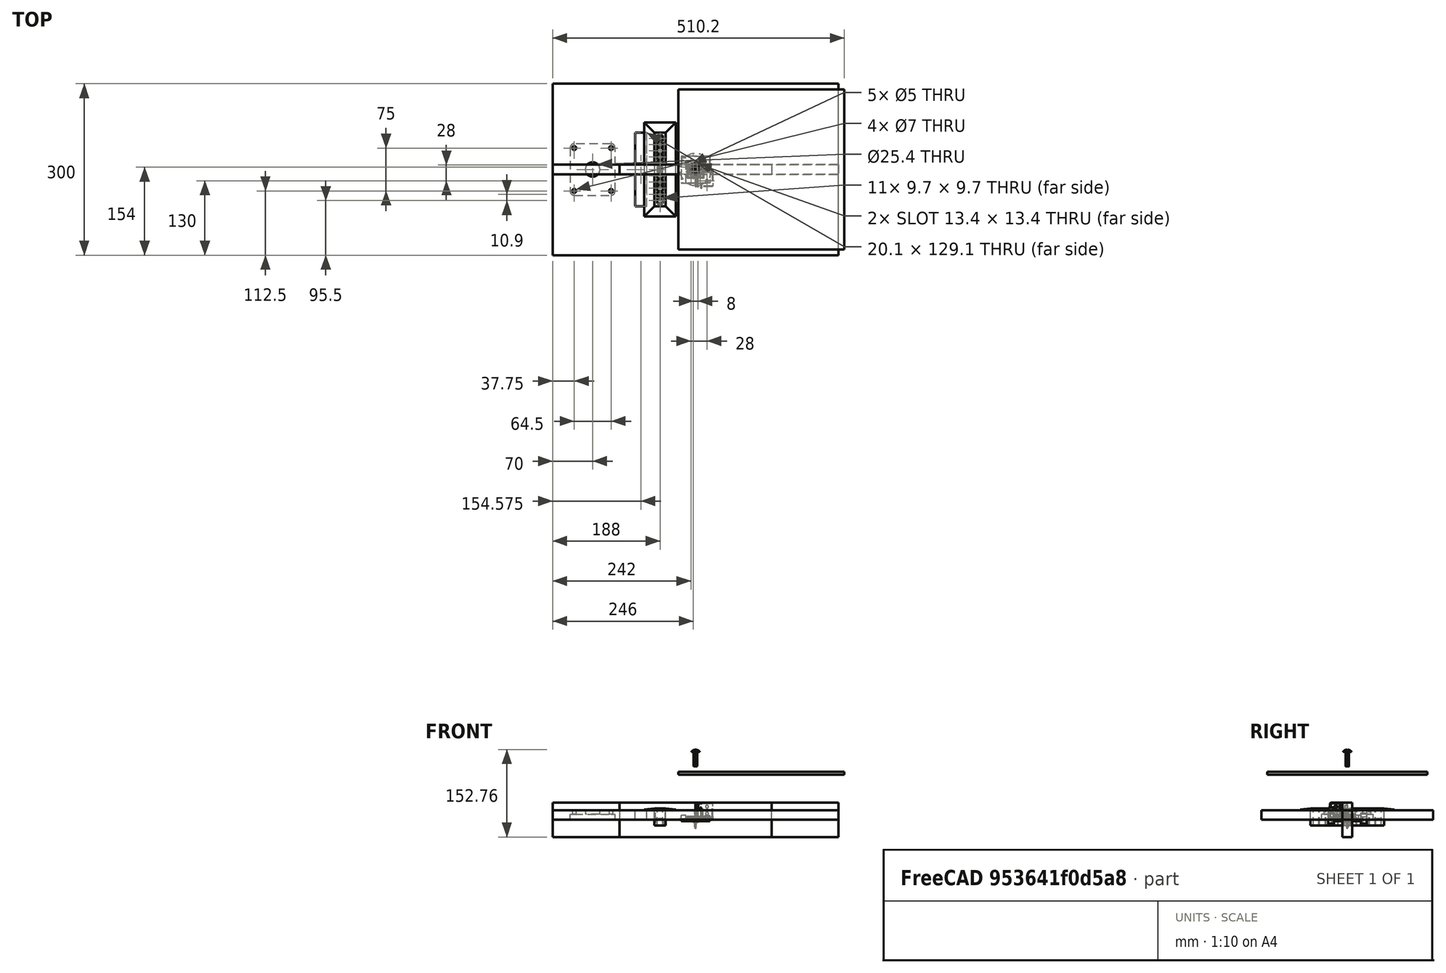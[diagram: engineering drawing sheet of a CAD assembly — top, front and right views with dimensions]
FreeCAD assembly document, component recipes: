
FREECAD ASSEMBLY — COMPONENT RECIPES ("BoxV2")

This assembly document has 71 components, labeled P0..P70 below (a component is one placed body or linked part). 9 of them carry a construction recipe — the FreeCAD feature program that regenerates the part from scratch, quoted from this document or its linked companion documents; the rest are supplied as boundary geometry only. No exploded tour is included for this assembly.
COMPONENT P0 — geometry summary ("Box_Cover002"; no construction recipe available for this part):
  bounding box: 500.0 x 300.0 x 17.0 mm
  tessellated surface: 2,508 triangles
  volume: 2430978 mm^3 (95% of its bounding box)
  symmetry: mirror-symmetric across its y mid-plane
COMPONENT P1 — recipe-attached ("Bracket002", modeled in this document).
Construction recipe (the document's own serialized feature program — sketch geometry with constraints, then the solid features built on it; lengths are millimeters unless a unit is written):

FEATURE [Sketcher::SketchObject] Sketch
  ArcFitTolerance = 1e-06
  AttachmentSupport = -> [XY_Plane]
  FullyConstrained = true
  MakeInternals = false
  MapMode = 5
  sketch-geometry (4):
    g0: LineSegment StartX=0 StartY=0 StartZ=0 EndX=30 EndY=0 EndZ=0
    g1: LineSegment StartX=30 StartY=0 StartZ=0 EndX=30 EndY=-30 EndZ=0
    g2: LineSegment StartX=30 StartY=-30 StartZ=0 EndX=0 EndY=-30 EndZ=0
    g3: LineSegment StartX=0 StartY=-30 StartZ=0 EndX=0 EndY=0 EndZ=0
  constraints (11):
    c: Coincident(g0,g1)
    c: Coincident(g1,g2)
    c: Coincident(g2,g3)
    c: Coincident(g3,g0)
    c: Horizontal(g0)
    c: Horizontal(g2)
    c: Vertical(g1)
    c: Vertical(g3)
    c: Distance(g1,g3) = 30
    c: Coincident(g0,g-1)
    c: DistanceY(g1,g1) = 30
FEATURE [PartDesign::Pad] Pad
  Direction = (0,0,1)
  Length = 30
  Length2 = 10
  Profile = -> Sketch
  ReferenceAxis = -> Sketch [N_Axis]
  Refine = true
  Suppressed = false
  Type = 0
FEATURE [PartDesign::Thickness] Thickness
  Base = -> Pad [Face2,Face3,Face6]
  BaseFeature = -> Pad
  Intersection = false
  Join = 0
  Mode = 0
  Refine = true
  Reversed = true
  SupportTransform = false
  Suppressed = false
  Value = 4
FEATURE [Sketcher::SketchObject] Sketch001
  ArcFitTolerance = 1e-06
  AttachmentOffset = pos=(0,2,0) rot=(0,0,1;0rad)
  AttachmentSupport = -> [YZ_Plane]
  FullyConstrained = true
  MakeInternals = false
  MapMode = 5
  Placement = pos=(0,0,2) rot=(0.57735,0.57735,0.57735;2.0944rad)
  expr: Constraints[1] = <<LHProperties>>.screw_diameter
  sketch-geometry (8):
    g0: Circle CenterX=-20 CenterY=21 CenterZ=0 NormalX=0 NormalY=0 NormalZ=1 AngleXU=0 Radius=2.5
    g1: Circle CenterX=-20 CenterY=9 CenterZ=0 NormalX=0 NormalY=0 NormalZ=1 AngleXU=0 Radius=2.5
    g2: LineSegment [constr] StartX=0 StartY=0 StartZ=0 EndX=0 EndY=30 EndZ=0
    g3: LineSegment [constr] StartX=0 StartY=30 StartZ=0 EndX=-30 EndY=30 EndZ=0
    g4: LineSegment [constr] StartX=-30 StartY=30 StartZ=0 EndX=-30 EndY=0 EndZ=0
    g5: LineSegment [constr] StartX=-30 StartY=0 StartZ=0 EndX=0 EndY=0 EndZ=0
    g6: LineSegment [constr] StartX=-20 StartY=21 StartZ=0 EndX=-20 EndY=30 EndZ=0
    g7: LineSegment [constr] StartX=-20 StartY=9 StartZ=0 EndX=-20 EndY=0 EndZ=0
  constraints (23):
    c: Equal(g1,g0)
    c: Diameter(g0) = 5
    c: Vertical(g0,g1)
    c: DistanceX(g1) = -20
    c: Coincident(g2,g3)
    c: Coincident(g3,g4)
    c: Coincident(g4,g5)
    c: Coincident(g5,g2)
    c: Vertical(g2)
    c: Vertical(g4)
    c: Horizontal(g3)
    c: Horizontal(g5)
    c: Coincident(g2,g-1)
    c: DistanceX(g3,g3) = 30
    c: DistanceY(g4,g4) = 30
    c: Coincident(g6,g0)
    c: PointOnObject(g6,g3)
    c: Vertical(g6)
    c: Coincident(g7,g1)
    c: PointOnObject(g7,g5)
    c: Vertical(g7)
    c: Equal(g7,g6)
    c: DistanceY(g1,g0) = 12
FEATURE [PartDesign::Pocket] Pocket
  BaseFeature = -> Thickness
  Direction = (-1,0,0)
  Length = 10
  Length2 = 5
  Midplane = true
  Profile = -> Sketch001
  ReferenceAxis = -> Sketch001 [N_Axis]
  Refine = true
  Suppressed = false
  Type = 0
FEATURE [PartDesign::PolarPattern] PolarPattern
  Angle = 90
  Axis = -> Sketch001 [V_Axis]
  BaseFeature = -> Pocket
  Mode = 0
  Occurrences = 2
  Offset = 120
  Originals = -> [Pocket]
  Refine = true
  Suppressed = false
  TransformMode = 0
FEATURE [PartDesign::SubtractiveCylinder] Cylinder
  Angle = 360
  AttacherType = Attacher::AttachEngine3D
  AttachmentOffset = pos=(20,-20,0) rot=(0,0,1;0rad)
  AttachmentSupport = -> [XY_Plane]
  BaseFeature = -> PolarPattern
  FirstAngle = 0
  Height = 10
  MapMode = 5
  Placement = pos=(20,-20,0) rot=(0,0,1;0rad)
  Radius = 2.5
  Refine = true
  SecondAngle = 0
  Suppressed = false
  expr: Radius = <<LHProperties>>.screw_diameter / 2
FEATURE [PartDesign::Chamfer] Chamfer
  Angle = 45
  Base = -> Cylinder [Edge35]
  BaseFeature = -> Cylinder
  ChamferType = 0
  FlipDirection = false
  Placement = pos=(20,-20,0) rot=(0,0,1;0rad)
  Refine = true
  Size = 8
  Size2 = 1
  SupportTransform = false
  Suppressed = false
  UseAllEdges = false
FEATURE [PartDesign::Chamfer] Chamfer001
  Angle = 45
  Base = -> Chamfer [Edge1,Edge2,Edge3,Edge4,Edge6,Edge8,Edge9,Edge10,Edge13,Edge14,Edge15,Edge16,Edge19,Edge20,Edge23,Edge24,Edge27,Edge30,Edge34,Edge35,Edge37,Edge38,Edge39]
  BaseFeature = -> Chamfer
  ChamferType = 0
  FlipDirection = false
  Placement = pos=(20,-20,0) rot=(0,0,1;0rad)
  Refine = true
  Size = 1
  Size2 = 1
  SupportTransform = false
  Suppressed = false
  UseAllEdges = false
FEATURE [PartDesign::Body] Body  label="Bracket"
  AllowCompound = false
  Group = -> [Sketch,Pad,Thickness,Sketch001,Pocket,PolarPattern,Cylinder,Chamfer,Chamfer001]
  Origin = -> Origin
  Tip = -> Chamfer001
COMPONENT P2 — same part as P1; its construction recipe is shown at P1.
COMPONENT P3 — same part as P1; its construction recipe is shown at P1.
COMPONENT P4 — same part as P1; its construction recipe is shown at P1.
COMPONENT P5 — recipe-attached ("Cable_Management002", modeled in this document).
Construction recipe (the document's own serialized feature program — sketch geometry with constraints, then the solid features built on it; lengths are millimeters unless a unit is written):

FEATURE [Sketcher::SketchObject] Sketch027
  ArcFitTolerance = 1e-06
  AttachmentSupport = -> [XY_Plane015]
  FullyConstrained = true
  MakeInternals = false
  MapMode = 5
  expr: Constraints[11] = <<CMProperties>>.cm_size
  sketch-geometry (5):
    g0: LineSegment StartX=-15 StartY=-15 StartZ=0 EndX=15 EndY=-15 EndZ=0
    g1: LineSegment StartX=15 StartY=-15 StartZ=0 EndX=15 EndY=15 EndZ=0
    g2: LineSegment StartX=15 StartY=15 StartZ=0 EndX=-15 EndY=15 EndZ=0
    g3: LineSegment StartX=-15 StartY=15 StartZ=0 EndX=-15 EndY=-15 EndZ=0
    g4: GeomPoint [constr] X=-1e-16 Y=0 Z=0
  constraints (12):
    c: Coincident(g0,g1)
    c: Coincident(g1,g2)
    c: Coincident(g2,g3)
    c: Coincident(g3,g0)
    c: Horizontal(g0)
    c: Horizontal(g2)
    c: Vertical(g1)
    c: Vertical(g3)
    c: Symmetric(g2,g0,g4)
    c: Coincident(g4,g-1)
    c: Equal(g2,g1)
    c: DistanceX(g2,g2) = 30
FEATURE [PartDesign::Pad] Pad013
  Direction = (0,0,1)
  Length = 4.7
  Length2 = 10
  Profile = -> Sketch027
  ReferenceAxis = -> Sketch027 [N_Axis]
  Refine = true
  Suppressed = false
  Type = 0
  expr: Length = <<CMProperties>>.cm_height + <<CMProperties>>.cm_base_height
FEATURE [Sketcher::SketchObject] Sketch028
  ArcFitTolerance = 1e-06
  AttachmentOffset = pos=(0,0,1.2) rot=(0,0,1;0rad)
  AttachmentSupport = -> [XY_Plane015]
  FullyConstrained = true
  MakeInternals = false
  MapMode = 5
  Placement = pos=(0,0,1.2) rot=(0,0,1;0rad)
  expr: .AttachmentOffset.Base.z = <<CMProperties>>.cm_base_height
  expr: Constraints[10] = <<CMProperties>>.cm_size / 2
  expr: Constraints[34] = <<CMProperties>>.cm_track_size
  expr: Constraints[9] = <<CMProperties>>.cm_size / 2
  sketch-geometry (19):
    g0: ArcOfCircle [constr] CenterX=-6 CenterY=6.01432 CenterZ=0 NormalX=0 NormalY=0 NormalZ=1 AngleXU=0 Radius=6.01432 StartAngle=4.71239 EndAngle=6.21417
    g1: ArcOfCircle [constr] CenterX=5.2375 CenterY=5.2375 CenterZ=0 NormalX=0 NormalY=0 NormalZ=1 AngleXU=0 Radius=5.25 StartAngle=4.78141 EndAngle=9.35576
    g2: LineSegment [constr] StartX=-6 StartY=0 StartZ=0 EndX=-15 EndY=0 EndZ=0
    g3: ArcOfCircle [constr] CenterX=6.01432 CenterY=-6 CenterZ=0 NormalX=0 NormalY=0 NormalZ=1 AngleXU=0 Radius=6.01432 StartAngle=1.63981 EndAngle=3.14159
    g4: LineSegment [constr] StartX=0 StartY=-6 StartZ=0 EndX=0 EndY=-15 EndZ=0
    g5: ArcOfCircle [constr] CenterX=-15 CenterY=0 CenterZ=0 NormalX=0 NormalY=0 NormalZ=-1 AngleXU=-3.14159 Radius=1.75 StartAngle=1.5708 EndAngle=4.71239
    g6: LineSegment StartX=-6 StartY=1.75 StartZ=0 EndX=-15 EndY=1.75 EndZ=0
    g7: ArcOfCircle CenterX=-6 CenterY=6.01432 CenterZ=0 NormalX=0 NormalY=0 NormalZ=1 AngleXU=0 Radius=4.26432 StartAngle=4.71239 EndAngle=6.21417
    g8: ArcOfCircle CenterX=5.2375 CenterY=5.2375 CenterZ=0 NormalX=0 NormalY=0 NormalZ=1 AngleXU=0 Radius=7 StartAngle=4.78141 EndAngle=9.35576
    g9: ArcOfCircle CenterX=6.01432 CenterY=-6 CenterZ=0 NormalX=0 NormalY=0 NormalZ=1 AngleXU=0 Radius=4.26432 StartAngle=1.63981 EndAngle=3.14159
    g10: LineSegment StartX=1.75 StartY=-6 StartZ=0 EndX=1.75 EndY=-15 EndZ=0
    g11: ArcOfCircle [constr] CenterX=0 CenterY=-15 CenterZ=0 NormalX=0 NormalY=0 NormalZ=-1 AngleXU=1.5708 Radius=1.75 StartAngle=1.5708 EndAngle=4.71239
    g12: LineSegment StartX=-1.75 StartY=-6 StartZ=0 EndX=-1.75 EndY=-15 EndZ=0
    g13: ArcOfCircle CenterX=6.01432 CenterY=-6 CenterZ=0 NormalX=0 NormalY=0 NormalZ=1 AngleXU=0 Radius=7.76432 StartAngle=1.63981 EndAngle=3.14159
    g14: ArcOfCircle CenterX=5.2375 CenterY=5.2375 CenterZ=0 NormalX=0 NormalY=0 NormalZ=1 AngleXU=0 Radius=3.5 StartAngle=4.78141 EndAngle=9.35576
    g15: ArcOfCircle CenterX=-6 CenterY=6.01432 CenterZ=0 NormalX=0 NormalY=0 NormalZ=1 AngleXU=0 Radius=7.76432 StartAngle=4.71239 EndAngle=6.21417
    g16: LineSegment StartX=-6 StartY=-1.75 StartZ=0 EndX=-15 EndY=-1.75 EndZ=0
    g17: LineSegment StartX=1.75 StartY=-15 StartZ=0 EndX=-1.75 EndY=-15 EndZ=0
    g18: LineSegment StartX=-15 StartY=1.75 StartZ=0 EndX=-15 EndY=-1.75 EndZ=0
  constraints (43):
    c: PointOnObject(g0,g-1)
    c: PointOnObject(g0,g-2)
    c: Tangent(g1,g0) = 1.5708
    c: PointOnObject(g2,g-1)
    c: Tangent(g2,g0) = 1.5708
    c: Vertical(g4)
    c: Tangent(g4,g3) = -1.5708
    c: Tangent(g3,g1) = 1.5708
    c: Vertical(g3,g-1)
    c: DistanceY(g4,g-1) = 15
    c: DistanceX(g2,g-1) = 15
    c: Tangent(g5,g6) = -1.5708
    c: Tangent(g5,g16) = 1.5708
    c: Tangent(g6,g7) = 1.5708
    c: Tangent(g7,g8) = 1.5708
    c: Tangent(g8,g9) = 1.5708
    c: Tangent(g9,g10) = -1.5708
    c: Tangent(g10,g11) = 1.5708
    c: Tangent(g11,g12) = -1.5708
    c: Tangent(g12,g13) = -1.5708
    c: Tangent(g13,g14) = 1.5708
    c: Tangent(g14,g15) = 1.5708
    c: Tangent(g15,g16) = 1.5708
    c: Coincident(g5,g2)
    c: Coincident(g1,g14)
    c: Coincident(g8,g1)
    c: Coincident(g0,g7)
    c: Coincident(g0,g15)
    c: Coincident(g3,g9)
    c: Coincident(g3,g13)
    c: Coincident(g11,g4)
    c: Horizontal(g10,g4)
    c: Horizontal(g11,g4)
    c: Vertical(g5,g2)
    c: DistanceY(g5,g5) = 3.5
    c: Equal(g6,g10)
    c: DistanceX(g0,g3) = 6
    c: Equal(g13,g15)
    c: Radius(g8) = 7
    c: Coincident(g17,g10)
    c: Coincident(g17,g11)
    c: Coincident(g18,g5)
    c: Coincident(g18,g5)
FEATURE [PartDesign::Pocket] Pocket011
  BaseFeature = -> Pad013
  Direction = (0,0,-1)
  Length = 5
  Length2 = 5
  Profile = -> Sketch028
  ReferenceAxis = -> Sketch028 [N_Axis]
  Refine = true
  Reversed = true
  Suppressed = false
  Type = 1
FEATURE [Sketcher::SketchObject] Sketch029
  ArcFitTolerance = 1e-06
  AttachmentOffset = pos=(0,0,4.7) rot=(0,0,1;0rad)
  AttachmentSupport = -> [XY_Plane015]
  FullyConstrained = true
  MakeInternals = false
  MapMode = 5
  Placement = pos=(0,0,4.7) rot=(0,0,1;0rad)
  expr: .AttachmentOffset.Base.z = <<CMProperties>>.cm_base_height + <<CMProperties>>.cm_height
  expr: Constraints[11] = Sketch027.Constraints[11]
  expr: Constraints[31] = Sketch028.Constraints[9]
  expr: Constraints[32] = Sketch028.Constraints[10]
  expr: Constraints[55] = <<CMProperties>>.cm_track_size
  sketch-geometry (41):
    g0: LineSegment [constr] StartX=-15 StartY=-15 StartZ=0 EndX=15 EndY=-15 EndZ=0
    g1: LineSegment [constr] StartX=15 StartY=-15 StartZ=0 EndX=15 EndY=15 EndZ=0
    g2: LineSegment [constr] StartX=15 StartY=15 StartZ=0 EndX=-15 EndY=15 EndZ=0
    g3: LineSegment [constr] StartX=-15 StartY=15 StartZ=0 EndX=-15 EndY=-15 EndZ=0
    g4: GeomPoint [constr] X=0 Y=0 Z=0
    g5: LineSegment StartX=15 StartY=-15 StartZ=0 EndX=15 EndY=15 EndZ=0
    g6: LineSegment StartX=15 StartY=15 StartZ=0 EndX=-15 EndY=15 EndZ=0
    g7: LineSegment StartX=13.4 StartY=-13.4 StartZ=0 EndX=13.4 EndY=13.4 EndZ=0
    g8: LineSegment StartX=13.4 StartY=13.4 StartZ=0 EndX=-13.4 EndY=13.4 EndZ=0
    g9: GeomPoint [constr] X=0 Y=0 Z=0
    g10: ArcOfCircle [constr] CenterX=-8 CenterY=8.06933 CenterZ=0 NormalX=0 NormalY=0 NormalZ=1 AngleXU=0 Radius=8.06933 StartAngle=4.71239 EndAngle=6.15201
    g11: ArcOfCircle [constr] CenterX=6.1963 CenterY=6.1963 CenterZ=0 NormalX=0 NormalY=0 NormalZ=1 AngleXU=0 Radius=6.25 StartAngle=4.84357 EndAngle=9.2936
    g12: LineSegment [constr] StartX=-8 StartY=0 StartZ=0 EndX=-15 EndY=0 EndZ=0
    g13: ArcOfCircle [constr] CenterX=8.06933 CenterY=-8 CenterZ=0 NormalX=0 NormalY=0 NormalZ=1 AngleXU=0 Radius=8.06933 StartAngle=1.70198 EndAngle=3.14159
    g14: LineSegment [constr] StartX=0 StartY=-8 StartZ=0 EndX=0 EndY=-15 EndZ=0
    g15: ArcOfCircle [constr] CenterX=-15 CenterY=0 CenterZ=0 NormalX=0 NormalY=0 NormalZ=-1 AngleXU=-3.14159 Radius=1.75 StartAngle=1.5708 EndAngle=4.71239
    g16: LineSegment [constr] StartX=-8 StartY=1.75 StartZ=0 EndX=-15 EndY=1.75 EndZ=0
    g17: ArcOfCircle [constr] CenterX=-8 CenterY=8.06933 CenterZ=0 NormalX=0 NormalY=0 NormalZ=1 AngleXU=0 Radius=6.31933 StartAngle=4.71239 EndAngle=6.15201
    g18: ArcOfCircle [constr] CenterX=6.1963 CenterY=6.1963 CenterZ=0 NormalX=0 NormalY=0 NormalZ=1 AngleXU=0 Radius=8 StartAngle=4.84357 EndAngle=9.2936
    g19: ArcOfCircle [constr] CenterX=8.06933 CenterY=-8 CenterZ=0 NormalX=0 NormalY=0 NormalZ=1 AngleXU=0 Radius=6.31933 StartAngle=1.70198 EndAngle=3.14159
    g20: LineSegment [constr] StartX=1.75 StartY=-8 StartZ=0 EndX=1.75 EndY=-15 EndZ=0
    g21: ArcOfCircle [constr] CenterX=0 CenterY=-15 CenterZ=0 NormalX=0 NormalY=0 NormalZ=-1 AngleXU=1.5708 Radius=1.75 StartAngle=1.5708 EndAngle=4.71239
    g22: LineSegment [constr] StartX=-1.75 StartY=-8 StartZ=0 EndX=-1.75 EndY=-15 EndZ=0
    g23: ArcOfCircle [constr] CenterX=8.06933 CenterY=-8 CenterZ=0 NormalX=0 NormalY=0 NormalZ=1 AngleXU=0 Radius=9.81933 StartAngle=1.70198 EndAngle=3.14159
    g24: ArcOfCircle [constr] CenterX=6.1963 CenterY=6.1963 CenterZ=0 NormalX=0 NormalY=0 NormalZ=1 AngleXU=0 Radius=4.5 StartAngle=4.84357 EndAngle=9.2936
    g25: ArcOfCircle [constr] CenterX=-8 CenterY=8.06933 CenterZ=0 NormalX=0 NormalY=0 NormalZ=1 AngleXU=0 Radius=9.81933 StartAngle=4.71239 EndAngle=6.15201
    g26: LineSegment [constr] StartX=-8 StartY=-1.75 StartZ=0 EndX=-15 EndY=-1.75 EndZ=0
    g27: LineSegment [constr] StartX=1.75 StartY=-15 StartZ=0 EndX=-1.75 EndY=-15 EndZ=0
    g28: LineSegment [constr] StartX=-15 StartY=1.75 StartZ=0 EndX=-15 EndY=-1.75 EndZ=0
    g29: LineSegment StartX=-15 StartY=1.75 StartZ=0 EndX=-13.4 EndY=1.75 EndZ=0
    g30: LineSegment StartX=13.4 StartY=-13.4 StartZ=0 EndX=1.75 EndY=-13.4 EndZ=0
    g31: LineSegment StartX=15 StartY=-15 StartZ=0 EndX=1.75 EndY=-15 EndZ=0
    g32: LineSegment StartX=-1.75 StartY=-15 StartZ=0 EndX=-15 EndY=-15 EndZ=0
    g33: LineSegment StartX=-15 StartY=-15 StartZ=0 EndX=-15 EndY=-1.75 EndZ=0
    g34: LineSegment StartX=-15 StartY=1.75 StartZ=0 EndX=-15 EndY=15 EndZ=0
    g35: LineSegment StartX=-13.4 StartY=13.4 StartZ=0 EndX=-13.4 EndY=1.75 EndZ=0
    g36: LineSegment StartX=-1.75 StartY=-13.4 StartZ=0 EndX=-13.4 EndY=-13.4 EndZ=0
    g37: LineSegment StartX=-13.4 StartY=-13.4 StartZ=0 EndX=-13.4 EndY=-1.75 EndZ=0
    g38: LineSegment StartX=-1.75 StartY=-13.4 StartZ=0 EndX=-1.75 EndY=-15 EndZ=0
    g39: LineSegment StartX=1.75 StartY=-15 StartZ=0 EndX=1.75 EndY=-13.4 EndZ=0
    g40: LineSegment StartX=-13.4 StartY=-1.75 StartZ=0 EndX=-15 EndY=-1.75 EndZ=0
  constraints (99):
    c: Coincident(g0,g1)
    c: Coincident(g1,g2)
    c: Coincident(g2,g3)
    c: Coincident(g3,g0)
    c: Horizontal(g0)
    c: Horizontal(g2)
    c: Vertical(g1)
    c: Vertical(g3)
    c: Symmetric(g2,g0,g4)
    c: Coincident(g4,g-1)
    c: Equal(g2,g1)
    c: DistanceX(g2,g2) = 30
    c: Coincident(g5,g6)
    c: Vertical(g5)
    c: Horizontal(g6)
    c: Coincident(g7,g8)
    c: Vertical(g7)
    c: Horizontal(g8)
    c: Symmetric(g7,g8,g9)
    c: Coincident(g9,g4)
    c: Equal(g8,g7)
    c: DistanceX(g7,g1) = 1.6
    c: PointOnObject(g10,g-1)
    c: PointOnObject(g10,g-2)
    c: Tangent(g11,g10) = 1.5708
    c: PointOnObject(g12,g-1)
    c: Tangent(g12,g10) = 1.5708
    c: Vertical(g14)
    c: Tangent(g14,g13) = -1.5708
    c: Tangent(g13,g11) = 1.5708
    c: Vertical(g13,g-1)
    c: DistanceY(g14,g-1) = 15
    c: DistanceX(g12,g-1) = 15
    c: Tangent(g15,g16) = -1.5708
    c: Tangent(g15,g26) = 1.5708
    c: Tangent(g16,g17) = 1.5708
    c: Tangent(g17,g18) = 1.5708
    c: Tangent(g18,g19) = 1.5708
    c: Tangent(g19,g20) = -1.5708
    c: Tangent(g20,g21) = 1.5708
    c: Tangent(g21,g22) = -1.5708
    c: Tangent(g22,g23) = -1.5708
    c: Tangent(g23,g24) = 1.5708
    c: Tangent(g24,g25) = 1.5708
    c: Tangent(g25,g26) = 1.5708
    c: Coincident(g15,g12)
    c: Coincident(g11,g24)
    c: Coincident(g18,g11)
    c: Coincident(g10,g17)
    c: Coincident(g10,g25)
    c: Coincident(g13,g19)
    c: Coincident(g13,g23)
    c: Coincident(g21,g14)
    c: Horizontal(g21,g14)
    c: Vertical(g15,g12) = 5
    c: DistanceY(g15,g15) = 3.5
    c: Equal(g16,g20) = 8
    c: DistanceX(g10,g13) = 8
    c: Equal(g23,g25) = 8
    c: Radius(g18) = 8
    c: Coincident(g27,g20)
    c: Coincident(g27,g21)
    c: Coincident(g28,g15)
    c: Coincident(g28,g15)
    c: Coincident(g29,g15)
    c: PointOnObject(g29,g16)
    c: Coincident(g30,g7)
    c: PointOnObject(g30,g20)
    c: Horizontal(g30)
    c: Coincident(g31,g5)
    c: Coincident(g31,g20)
    c: Horizontal(g31)
    c: Coincident(g32,g21)
    c: Coincident(g32,g0)
    c: Coincident(g33,g0)
    c: Coincident(g33,g15)
    c: Coincident(g34,g15)
    c: Coincident(g34,g6)
    c: Vertical(g34)
    c: Coincident(g35,g8)
    c: Coincident(g35,g29)
    c: Vertical(g35)
    c: PointOnObject(g36,g22)
    c: Horizontal(g36)
    c: Coincident(g37,g36)
    c: PointOnObject(g37,g26)
    c: Vertical(g37)
    c: Vertical(g37,g29)
    c: Horizontal(g36,g30)
    c: Coincident(g38,g36)
    c: Coincident(g38,g21)
    c: Coincident(g39,g30)
    c: Vertical(g39)
    c: Tangent(g39,g21)
    c: Coincident(g40,g37)
    c: Coincident(g40,g15)
    c: Equal(g5,g6)
    c: Equal(g6,g2)
    c: PointOnObject(g39,g31)
FEATURE [PartDesign::Pad] Pad014
  BaseFeature = -> Pocket011
  Direction = (0,0,1)
  Length = 1.2
  Length2 = 10
  Profile = -> Sketch029
  ReferenceAxis = -> Sketch029 [N_Axis]
  Refine = true
  Suppressed = false
  Type = 0
  expr: Length = <<CMProperties>>.cover_thickness
FEATURE [Sketcher::SketchObject] Sketch031
  ArcFitTolerance = 1e-06
  AttachmentSupport = -> [XY_Plane015]
  FullyConstrained = true
  MakeInternals = false
  MapMode = 5
  expr: Constraints[0] = <<LHProperties>>.screw_diameter
  sketch-geometry (1):
    g0: Circle CenterX=-8 CenterY=-8 CenterZ=0 NormalX=0 NormalY=0 NormalZ=1 AngleXU=0 Radius=2.5
  constraints (3):
    c: Diameter(g0) = 5
    c: DistanceX(g0,g-1) = 8
    c: DistanceY(g0,g-1) = 8
FEATURE [PartDesign::Pocket] Pocket012
  BaseFeature = -> Pad014
  Direction = (0,0,-1)
  Length = 5
  Length2 = 5
  Profile = -> Sketch031
  ReferenceAxis = -> Sketch031 [N_Axis]
  Refine = true
  Reversed = true
  Suppressed = false
  Type = 1
FEATURE [PartDesign::Mirrored] Mirrored004
  BaseFeature = -> Pocket012
  MirrorPlane = -> Sketch031 [V_Axis]
  Originals = -> [Pocket012]
  Refine = true
  Suppressed = false
  TransformMode = 0
FEATURE [PartDesign::Mirrored] Mirrored005
  BaseFeature = -> Mirrored004
  MirrorPlane = -> Sketch031 [H_Axis]
  Originals = -> [Pocket012]
  Refine = true
  Suppressed = false
  TransformMode = 0
FEATURE [PartDesign::Body] Body013  label="Cable_Management"
  AllowCompound = false
  Group = -> [Sketch027,Pad013,Sketch028,Pocket011,Sketch029,Pad014,Sketch031,Pocket012,Mirrored004,Mirrored005]
  Origin = -> Origin015
  Tip = -> Mirrored005
COMPONENT P6 — same part as P5; its construction recipe is shown at P5.
COMPONENT P7 — recipe-attached ("Cable_Management_Cover002", modeled in this document).
Construction recipe (the document's own serialized feature program — sketch geometry with constraints, then the solid features built on it; lengths are millimeters unless a unit is written):

FEATURE [Sketcher::SketchObject] Sketch030
  ArcFitTolerance = 1e-06
  AttachmentSupport = -> [XY_Plane016]
  FullyConstrained = true
  MakeInternals = false
  MapMode = 5
  expr: Constraints[11] = <<CMProperties>>.cm_cover_size
  expr: Constraints[14] = <<LHProperties>>.screw_diameter
  expr: Constraints[71] = <<LHProperties>>.screw_diameter
  sketch-geometry (29):
    g0: LineSegment StartX=-13.2 StartY=-13.2 StartZ=0 EndX=13.2 EndY=-13.2 EndZ=0
    g1: LineSegment StartX=13.2 StartY=-13.2 StartZ=0 EndX=13.2 EndY=13.2 EndZ=0
    g2: LineSegment StartX=13.2 StartY=13.2 StartZ=0 EndX=-13.2 EndY=13.2 EndZ=0
    g3: LineSegment StartX=-13.2 StartY=13.2 StartZ=0 EndX=-13.2 EndY=-13.2 EndZ=0
    g4: GeomPoint [constr] X=0 Y=0 Z=0
    g5: Circle CenterX=-8 CenterY=-8 CenterZ=0 NormalX=0 NormalY=0 NormalZ=1 AngleXU=0 Radius=2.5
    g6: ArcOfCircle CenterX=-9.2 CenterY=6.8 CenterZ=0 NormalX=0 NormalY=0 NormalZ=1 AngleXU=0 Radius=1.5 StartAngle=2.35619 EndAngle=5.49779
    g7: ArcOfCircle CenterX=-6.8 CenterY=9.2 CenterZ=0 NormalX=0 NormalY=0 NormalZ=1 AngleXU=0 Radius=1.5 StartAngle=5.49779 EndAngle=8.63938
    g8: LineSegment StartX=-10.2607 StartY=7.86066 StartZ=0 EndX=-7.86066 EndY=10.2607 EndZ=0
    g9: LineSegment StartX=-8.13934 StartY=5.73934 StartZ=0 EndX=-5.73934 EndY=8.13934 EndZ=0
    g10: ArcOfCircle CenterX=-9.2 CenterY=-1.2 CenterZ=0 NormalX=0 NormalY=0 NormalZ=1 AngleXU=0 Radius=1.5 StartAngle=2.35619 EndAngle=5.49779
    g11: ArcOfCircle CenterX=1.2 CenterY=9.2 CenterZ=0 NormalX=0 NormalY=0 NormalZ=1 AngleXU=0 Radius=1.5 StartAngle=5.49779 EndAngle=8.63938
    g12: LineSegment StartX=-10.2607 StartY=-0.13934 StartZ=0 EndX=0.13934 EndY=10.2607 EndZ=0
    g13: LineSegment StartX=-8.13934 StartY=-2.26066 StartZ=0 EndX=2.26066 EndY=8.13934 EndZ=0
    g14: ArcOfCircle [constr] CenterX=-9.2 CenterY=-9.2 CenterZ=0 NormalX=0 NormalY=0 NormalZ=1 AngleXU=0 Radius=1.5 StartAngle=2.35619 EndAngle=5.49779
    g15: ArcOfCircle CenterX=9.2 CenterY=9.2 CenterZ=0 NormalX=0 NormalY=0 NormalZ=1 AngleXU=0 Radius=1.5 StartAngle=5.49779 EndAngle=8.63938
    g16: LineSegment [constr] StartX=-10.2607 StartY=-8.13934 StartZ=0 EndX=8.13934 EndY=10.2607 EndZ=0
    g17: LineSegment [constr] StartX=-8.13934 StartY=-10.2607 StartZ=0 EndX=10.2607 EndY=8.13934 EndZ=0
    g18: ArcOfCircle CenterX=-1.2 CenterY=-9.2 CenterZ=0 NormalX=0 NormalY=0 NormalZ=1 AngleXU=0 Radius=1.5 StartAngle=2.35619 EndAngle=5.49779
    g19: ArcOfCircle CenterX=9.2 CenterY=1.2 CenterZ=0 NormalX=0 NormalY=0 NormalZ=1 AngleXU=0 Radius=1.5 StartAngle=5.49779 EndAngle=8.63938
    g20: LineSegment StartX=-2.26066 StartY=-8.13934 StartZ=0 EndX=8.13934 EndY=2.26066 EndZ=0
    g21: LineSegment StartX=-0.13934 StartY=-10.2607 StartZ=0 EndX=10.2607 EndY=0.13934 EndZ=0
    g22: ArcOfCircle CenterX=6.8 CenterY=-9.2 CenterZ=0 NormalX=0 NormalY=0 NormalZ=1 AngleXU=0 Radius=1.5 StartAngle=2.35619 EndAngle=5.49779
    g23: ArcOfCircle CenterX=9.2 CenterY=-6.8 CenterZ=0 NormalX=0 NormalY=0 NormalZ=1 AngleXU=0 Radius=1.5 StartAngle=5.49779 EndAngle=8.63938
    g24: LineSegment StartX=5.73934 StartY=-8.13934 StartZ=0 EndX=8.13934 EndY=-5.73934 EndZ=0
    g25: LineSegment StartX=7.86066 StartY=-10.2607 StartZ=0 EndX=10.2607 EndY=-7.86066 EndZ=0
    g26: LineSegment StartX=8.13934 StartY=10.2607 StartZ=0 EndX=-5.68798 EndY=-3.56666 EndZ=0
    g27: LineSegment StartX=10.2607 StartY=8.13934 StartZ=0 EndX=-3.56666 EndY=-5.68798 EndZ=0
    g28: ArcOfCircle CenterX=-8 CenterY=-8 CenterZ=0 NormalX=0 NormalY=0 NormalZ=1 AngleXU=0 Radius=5 StartAngle=0.480706 EndAngle=1.09009
  constraints (72):
    c: Coincident(g0,g1)
    c: Coincident(g1,g2)
    c: Coincident(g2,g3)
    c: Coincident(g3,g0)
    c: Horizontal(g0)
    c: Horizontal(g2)
    c: Vertical(g1)
    c: Vertical(g3)
    c: Symmetric(g2,g0,g4)
    c: Coincident(g4,g-1)
    c: Equal(g2,g1)
    c: DistanceX(g2,g2) = 26.4
    c: DistanceX(g5,g4) = 8
    c: DistanceY(g5,g4) = 8
    c: Diameter(g5) = 5
    c: Tangent(g6,g8) = 1.5708
    c: Tangent(g6,g9) = -1.5708
    c: Tangent(g7,g8) = 1.5708
    c: Tangent(g7,g9) = -1.5708
    c: Equal(g6,g7)
    c: Tangent(g10,g12) = 1.5708
    c: Tangent(g10,g13) = -1.5708
    c: Tangent(g11,g12) = 1.5708
    c: Tangent(g11,g13) = -1.5708
    c: Equal(g10,g11)
    c: Tangent(g14,g16) = 1.5708
    c: Tangent(g14,g17) = -1.5708
    c: Tangent(g15,g16) = 1.5708
    c: Tangent(g15,g17) = -1.5708
    c: Equal(g14,g15)
    c: Tangent(g18,g20) = 1.5708
    c: Tangent(g18,g21) = -1.5708
    c: Tangent(g19,g20) = 1.5708
    c: Tangent(g19,g21) = -1.5708
    c: Equal(g18,g19)
    c: Tangent(g22,g24) = 1.5708
    c: Tangent(g22,g25) = -1.5708
    c: Tangent(g23,g24) = 1.5708
    c: Tangent(g23,g25) = -1.5708
    c: Equal(g22,g23)
    c: Symmetric(g15,g14,g4)
    c: Distance(g15,g15) = 3
    c: Equal(g19,g23)
    c: Equal(g23,g11)
    c: Equal(g11,g7)
    c: Equal(g7,g15)
    c: Horizontal(g15,g11)
    c: Horizontal(g11,g7)
    c: Horizontal(g14,g18)
    c: Horizontal(g14,g22)
    c: Vertical(g14,g10)
    c: Vertical(g14,g6)
    c: Vertical(g15,g19)
    c: Vertical(g15,g23)
    c: Parallel(g9,g13)
    c: Parallel(g13,g17)
    c: Parallel(g17,g21)
    c: Parallel(g21,g25)
    c: DistanceX(g11,g15) = 8
    c: DistanceX(g7,g11) = 8
    c: DistanceY(g19,g15) = 8
    c: DistanceY(g23,g19) = 8
    c: Angle(g-1,g17) = 0.785398
    c: DistanceX(g15,g1) = 4
    c: Coincident(g26,g15)
    c: PointOnObject(g26,g16)
    c: Coincident(g27,g15)
    c: PointOnObject(g27,g17)
    c: Coincident(g28,g5)
    c: Coincident(g28,g27)
    c: Coincident(g28,g26)
    c: Radius(g28) = 5
FEATURE [PartDesign::Pad] Pad015
  Direction = (0,0,1)
  Length = 1.2
  Length2 = 10
  Profile = -> Sketch030
  ReferenceAxis = -> Sketch030 [N_Axis]
  Refine = true
  Suppressed = false
  Type = 0
  expr: Length = <<CMProperties>>.cover_thickness
FEATURE [PartDesign::Body] Body014  label="Cable_Management_Cover"
  AllowCompound = false
  Group = -> [Sketch030,Pad015]
  Origin = -> Origin016
  Tip = -> Pad015
COMPONENT P8 — same part as P7; its construction recipe is shown at P7.
COMPONENT P9 — geometry summary ("Foam_Pad002"; no construction recipe available for this part):
  bounding box: 290.0 x 280.0 x 5.0 mm
  tessellated surface: 12 triangles
  volume: 406000 mm^3 (100% of its bounding box)
  symmetry: 2-fold rotationally symmetric about the x axis; 2-fold rotationally symmetric about the y axis; 2-fold rotationally symmetric about the z axis; mirror-symmetric across its x mid-plane, y mid-plane, z mid-plane
COMPONENT P10 — geometry summary ("Foot002"; no construction recipe available for this part):
  bounding box: 27.0 x 27.0 x 6.0 mm
  tessellated surface: 11,796 triangles
  volume: 2458 mm^3 (56% of its bounding box)
  symmetry: revolution-symmetric about the z axis through its bounding-box center; mirror-symmetric across its x mid-plane, y mid-plane
COMPONENT P11 — geometry summary ("Foot003"; no construction recipe available for this part):
  bounding box: 27.0 x 27.0 x 6.0 mm
  tessellated surface: 11,796 triangles
  volume: 2458 mm^3 (56% of its bounding box)
  symmetry: revolution-symmetric about the z axis through its bounding-box center; mirror-symmetric across its x mid-plane, y mid-plane
COMPONENT P12 — geometry summary ("Foot004"; no construction recipe available for this part):
  bounding box: 27.0 x 27.0 x 6.0 mm
  tessellated surface: 11,796 triangles
  volume: 2458 mm^3 (56% of its bounding box)
  symmetry: revolution-symmetric about the z axis through its bounding-box center; mirror-symmetric across its x mid-plane, y mid-plane
COMPONENT P13 — geometry summary ("Foot005"; no construction recipe available for this part):
  bounding box: 27.0 x 27.0 x 6.0 mm
  tessellated surface: 11,796 triangles
  volume: 2458 mm^3 (56% of its bounding box)
  symmetry: revolution-symmetric about the z axis through its bounding-box center; mirror-symmetric across its x mid-plane, y mid-plane
COMPONENT P14 — geometry summary ("Joystick_hole_cover002"; no construction recipe available for this part):
  bounding box: 56.0 x 56.0 x 1.6 mm
  tessellated surface: 1,008 triangles
  volume: 3619 mm^3 (72% of its bounding box)
  symmetry: 2-fold rotationally symmetric about the x axis; revolution-symmetric about the z axis through its bounding-box center; mirror-symmetric across its y mid-plane, z mid-plane
COMPONENT P15 — recipe-attached ("LED_Array002", modeled in this document).
Construction recipe (the document's own serialized feature program — sketch geometry with constraints, then the solid features built on it; lengths are millimeters unless a unit is written):

FEATURE [PartDesign::AdditiveCylinder] Cylinder003
  Angle = 360
  AttacherType = Attacher::AttachEngine3D
  AttachmentOffset = pos=(0,54.5,0) rot=(0,0,1;0rad)
  AttachmentSupport = -> [XY_Plane021]
  FirstAngle = 0
  Height = 1.2
  MapMode = 5
  Placement = pos=(0,54.5,0) rot=(0,0,1;0rad)
  Radius = 4.85
  Refine = true
  SecondAngle = 0
  Suppressed = false
  expr: .AttachmentOffset.Base.y = -<<LHProperties>>.led_dim / 2 + <<LHProperties>>.led_housing_base_length / 2 - <<LHProperties>>.led_array_housing_spacing
FEATURE [Sketcher::SketchObject] Sketch037
  ArcFitTolerance = 1e-06
  AttachmentSupport = -> [XY_Plane021]
  ExternalGeometry = -> [Cylinder003]
  FullyConstrained = true
  MakeInternals = false
  MapMode = 5
  sketch-geometry (13):
    g0: LineSegment StartX=-4 StartY=54.5 StartZ=0 EndX=-4 EndY=-54.5 EndZ=0
    g1: LineSegment StartX=-4 StartY=-54.5 StartZ=0 EndX=-2.5 EndY=-54.5 EndZ=0
    g2: LineSegment StartX=-2.5 StartY=-54.5 StartZ=0 EndX=-2.5 EndY=54.5 EndZ=0
    g3: LineSegment StartX=-2.5 StartY=54.5 StartZ=0 EndX=-4 EndY=54.5 EndZ=0
    g4: LineSegment StartX=4 StartY=54.5 StartZ=0 EndX=4 EndY=-54.5 EndZ=0
    g5: LineSegment StartX=4 StartY=-54.5 StartZ=0 EndX=2.5 EndY=-54.5 EndZ=0
    g6: LineSegment StartX=2.5 StartY=-54.5 StartZ=0 EndX=2.5 EndY=54.5 EndZ=0
    g7: LineSegment StartX=2.5 StartY=54.5 StartZ=0 EndX=4 EndY=54.5 EndZ=0
    g8: LineSegment StartX=0.75 StartY=-54.5 StartZ=0 EndX=0.75 EndY=54.5 EndZ=0
    g9: LineSegment StartX=0.75 StartY=54.5 StartZ=0 EndX=-0.75 EndY=54.5 EndZ=0
    g10: LineSegment StartX=-0.75 StartY=54.5 StartZ=0 EndX=-0.75 EndY=-54.5 EndZ=0
    g11: LineSegment StartX=-0.75 StartY=-54.5 StartZ=0 EndX=0.75 EndY=-54.5 EndZ=0
    g12: GeomPoint [constr] X=0 Y=0 Z=0
  constraints (35):
    c: Coincident(g0,g1)
    c: Coincident(g1,g2)
    c: Coincident(g2,g3)
    c: Coincident(g3,g0)
    c: Vertical(g0)
    c: Vertical(g2)
    c: Horizontal(g1)
    c: Horizontal(g3)
    c: Coincident(g4,g5)
    c: Coincident(g5,g6)
    c: Coincident(g6,g7)
    c: Coincident(g7,g4)
    c: Vertical(g4)
    c: Horizontal(g5)
    c: Horizontal(g7)
    c: Equal(g4,g2)
    c: Equal(g7,g3)
    c: Horizontal(g2,g-3)
    c: Horizontal(g4,g-3)
    c: DistanceX(g3,g3) = 1.5
    c: DistanceX(g0,g-3) = 4
    c: DistanceX(g-3,g4) = 4
    c: Symmetric(g6,g5,g-1)
    c: Coincident(g8,g9)
    c: Coincident(g9,g10)
    c: Coincident(g10,g11)
    c: Coincident(g11,g8)
    c: Vertical(g8)
    c: Vertical(g10)
    c: Horizontal(g9)
    c: Horizontal(g11)
    c: Symmetric(g10,g8,g12)
    c: Coincident(g12,g-1)
    c: PointOnObject(g-3,g9)
    c: Equal(g9,g3)
FEATURE [PartDesign::Pad] Pad020
  BaseFeature = -> Cylinder003
  Direction = (0,0,1)
  Length = 1
  Length2 = 10
  Placement = pos=(0,54.5,0) rot=(0,0,1;0rad)
  Profile = -> Sketch037
  ReferenceAxis = -> Sketch037 [N_Axis]
  Refine = true
  Reversed = true
  Suppressed = false
  Type = 0
FEATURE [PartDesign::AdditiveBox] Box001
  AttacherType = Attacher::AttachEngine3D
  AttachmentOffset = pos=(-2.5,52,1) rot=(0,0,1;0rad)
  AttachmentSupport = -> [XY_Plane021]
  BaseFeature = -> Pad020
  Height = 1.5
  Length = 5
  MapMode = 5
  Placement = pos=(-2.5,52,1) rot=(0,0,1;0rad)
  Refine = true
  Suppressed = false
  Width = 5
  expr: .AttachmentOffset.Base.y = -<<LHProperties>>.led_dim / 2 + <<LHProperties>>.led_housing_base_length / 2 - <<LHProperties>>.led_array_housing_spacing - 2.5
FEATURE [PartDesign::LinearPattern] LinearPattern002
  BaseFeature = -> Box001
  Direction = -> Y_Axis021
  Length = 109
  Mode = 1
  Occurrences = 11
  Offset = 10.9
  Originals = -> [Cylinder003,Box001]
  Placement = pos=(-2.5,52,1) rot=(0,0,1;0rad)
  Refine = true
  Reversed = true
  Suppressed = false
  TransformMode = 0
  expr: Length = <<LHProperties>>.led_array_spacing
  expr: Occurrences = <<LHProperties>>.led_amount
  expr: Offset = <<LHProperties>>.led_array_spacing + <<LHProperties>>.led_dim
FEATURE [PartDesign::Body] Body019  label="LED_Array"
  AllowCompound = false
  Group = -> [Cylinder003,Sketch037,Pad020,Box001,LinearPattern002]
  Origin = -> Origin021
  Placement = pos=(-62,-3e-16,0) rot=(0,0,1;0rad)
  Tip = -> Box001
COMPONENT P16 — geometry summary ("LED_Housing002"; no construction recipe available for this part):
  bounding box: 164.0 x 55.0 x 30.0 mm
  tessellated surface: 352 triangles
  volume: 55470 mm^3 (20% of its bounding box)
  symmetry: 2-fold rotationally symmetric about the z axis; mirror-symmetric across its x mid-plane, y mid-plane
COMPONENT P17 — geometry summary ("LED_Housing_Cube002"; no construction recipe available for this part):
  bounding box: 9.7 x 9.7 x 8.0 mm
  tessellated surface: 12 triangles
  volume: 753 mm^3 (100% of its bounding box)
  symmetry: 2-fold rotationally symmetric about the y axis; 4-fold rotationally symmetric about the z axis; mirror-symmetric across its y mid-plane, z mid-plane
COMPONENT P18 — geometry summary ("LED_Housing_Cube003"; no construction recipe available for this part):
  bounding box: 9.7 x 9.7 x 8.0 mm
  tessellated surface: 12 triangles
  volume: 753 mm^3 (100% of its bounding box)
  symmetry: 2-fold rotationally symmetric about the y axis; 4-fold rotationally symmetric about the z axis; mirror-symmetric across its y mid-plane, z mid-plane
COMPONENT P19 — geometry summary ("LED_Housing_Cube004"; no construction recipe available for this part):
  bounding box: 9.7 x 9.7 x 8.0 mm
  tessellated surface: 12 triangles
  volume: 753 mm^3 (100% of its bounding box)
  symmetry: 2-fold rotationally symmetric about the y axis; 4-fold rotationally symmetric about the z axis; mirror-symmetric across its y mid-plane, z mid-plane
COMPONENT P20 — geometry summary ("LED_Housing_Cube005"; no construction recipe available for this part):
  bounding box: 9.7 x 9.7 x 8.0 mm
  tessellated surface: 12 triangles
  volume: 753 mm^3 (100% of its bounding box)
  symmetry: 2-fold rotationally symmetric about the y axis; 4-fold rotationally symmetric about the z axis; mirror-symmetric across its y mid-plane, z mid-plane
COMPONENT P21 — geometry summary ("LED_Housing_Cube006"; no construction recipe available for this part):
  bounding box: 9.7 x 9.7 x 8.0 mm
  tessellated surface: 12 triangles
  volume: 753 mm^3 (100% of its bounding box)
  symmetry: 2-fold rotationally symmetric about the y axis; 4-fold rotationally symmetric about the z axis; mirror-symmetric across its y mid-plane, z mid-plane
COMPONENT P22 — geometry summary ("LED_Housing_Cube007"; no construction recipe available for this part):
  bounding box: 9.7 x 9.7 x 8.0 mm
  tessellated surface: 12 triangles
  volume: 753 mm^3 (100% of its bounding box)
  symmetry: 2-fold rotationally symmetric about the y axis; 4-fold rotationally symmetric about the z axis; mirror-symmetric across its y mid-plane, z mid-plane
COMPONENT P23 — geometry summary ("LED_Housing_Cube008"; no construction recipe available for this part):
  bounding box: 9.7 x 9.7 x 8.0 mm
  tessellated surface: 12 triangles
  volume: 753 mm^3 (100% of its bounding box)
  symmetry: 2-fold rotationally symmetric about the y axis; 4-fold rotationally symmetric about the z axis; mirror-symmetric across its y mid-plane, z mid-plane
COMPONENT P24 — geometry summary ("LED_Housing_Cube009"; no construction recipe available for this part):
  bounding box: 9.7 x 9.7 x 8.0 mm
  tessellated surface: 12 triangles
  volume: 753 mm^3 (100% of its bounding box)
  symmetry: 2-fold rotationally symmetric about the y axis; 4-fold rotationally symmetric about the z axis; mirror-symmetric across its y mid-plane, z mid-plane
COMPONENT P25 — geometry summary ("LED_Housing_Cube010"; no construction recipe available for this part):
  bounding box: 9.7 x 9.7 x 8.0 mm
  tessellated surface: 12 triangles
  volume: 753 mm^3 (100% of its bounding box)
  symmetry: 2-fold rotationally symmetric about the y axis; 4-fold rotationally symmetric about the z axis; mirror-symmetric across its y mid-plane, z mid-plane
COMPONENT P26 — geometry summary ("LED_Housing_Cube011"; no construction recipe available for this part):
  bounding box: 9.7 x 9.7 x 8.0 mm
  tessellated surface: 12 triangles
  volume: 753 mm^3 (100% of its bounding box)
  symmetry: 2-fold rotationally symmetric about the y axis; 4-fold rotationally symmetric about the z axis; mirror-symmetric across its y mid-plane, z mid-plane
COMPONENT P27 — geometry summary ("LED_Housing_Cube012"; no construction recipe available for this part):
  bounding box: 9.7 x 9.7 x 8.0 mm
  tessellated surface: 12 triangles
  volume: 753 mm^3 (100% of its bounding box)
  symmetry: 2-fold rotationally symmetric about the y axis; 4-fold rotationally symmetric about the z axis; mirror-symmetric across its y mid-plane, z mid-plane
COMPONENT P28 — geometry summary ("Latch002"; no construction recipe available for this part):
  bounding box: 21.8 x 8.0 x 2.6 mm
  tessellated surface: 80 triangles
  volume: 276 mm^3 (60% of its bounding box)
  symmetry: mirror-symmetric across its y mid-plane
COMPONENT P29 — geometry summary ("Latch003"; no construction recipe available for this part):
  bounding box: 21.8 x 8.0 x 2.6 mm
  tessellated surface: 80 triangles
  volume: 276 mm^3 (60% of its bounding box)
  symmetry: mirror-symmetric across its y mid-plane
COMPONENT P30 — geometry summary ("Latch004"; no construction recipe available for this part):
  bounding box: 21.8 x 8.0 x 2.6 mm
  tessellated surface: 80 triangles
  volume: 276 mm^3 (60% of its bounding box)
  symmetry: mirror-symmetric across its y mid-plane
COMPONENT P31 — geometry summary ("Latch005"; no construction recipe available for this part):
  bounding box: 21.8 x 8.0 x 2.6 mm
  tessellated surface: 80 triangles
  volume: 276 mm^3 (60% of its bounding box)
  symmetry: mirror-symmetric across its y mid-plane
COMPONENT P32 — geometry summary ("ProtoBoard002"; no construction recipe available for this part):
  bounding box: 50.0 x 47.0 x 10.0 mm
  tessellated surface: 36 triangles
  volume: 8633 mm^3 (37% of its bounding box)
COMPONENT P33 — geometry summary ("Wall_Long002"; no construction recipe available for this part):
  bounding box: 500.0 x 60.0 x 17.0 mm
  tessellated surface: 12 triangles
  volume: 510000 mm^3 (100% of its bounding box)
  symmetry: 2-fold rotationally symmetric about the x axis; 2-fold rotationally symmetric about the y axis; mirror-symmetric across its z mid-plane
COMPONENT P34 — geometry summary ("Wall_Long003"; no construction recipe available for this part):
  bounding box: 500.0 x 60.0 x 17.0 mm
  tessellated surface: 12 triangles
  volume: 510000 mm^3 (100% of its bounding box)
  symmetry: 2-fold rotationally symmetric about the x axis; 2-fold rotationally symmetric about the y axis; mirror-symmetric across its z mid-plane
COMPONENT P35 — geometry summary ("Wall_Short002"; no construction recipe available for this part):
  bounding box: 266.0 x 60.0 x 17.0 mm
  tessellated surface: 12 triangles
  volume: 271320 mm^3 (100% of its bounding box)
  symmetry: 2-fold rotationally symmetric about the x axis; 2-fold rotationally symmetric about the y axis; 2-fold rotationally symmetric about the z axis; mirror-symmetric across its y mid-plane, z mid-plane
COMPONENT P36 — geometry summary ("Wall_Short003"; no construction recipe available for this part):
  bounding box: 266.0 x 60.0 x 17.0 mm
  tessellated surface: 12 triangles
  volume: 271320 mm^3 (100% of its bounding box)
  symmetry: 2-fold rotationally symmetric about the x axis; 2-fold rotationally symmetric about the y axis; 2-fold rotationally symmetric about the z axis; mirror-symmetric across its y mid-plane, z mid-plane
COMPONENT P37 — geometry summary ("#5x5/8in-Screw026"; no construction recipe available for this part):
  bounding box: 15.9 x 6.0 x 6.0 mm
  tessellated surface: 3,812 triangles
  volume: 103 mm^3 (18% of its bounding box)
COMPONENT P38 — geometry summary ("#5x5/8in-Screw002"; no construction recipe available for this part):
  bounding box: 15.9 x 6.0 x 6.0 mm
  tessellated surface: 3,812 triangles
  volume: 103 mm^3 (18% of its bounding box)
COMPONENT P39 — geometry summary ("#5x5/8in-Screw003"; no construction recipe available for this part):
  bounding box: 15.9 x 6.0 x 6.0 mm
  tessellated surface: 3,812 triangles
  volume: 103 mm^3 (18% of its bounding box)
COMPONENT P40 — geometry summary ("#5x5/8in-Screw004"; no construction recipe available for this part):
  bounding box: 15.9 x 6.0 x 6.0 mm
  tessellated surface: 3,812 triangles
  volume: 103 mm^3 (18% of its bounding box)
COMPONENT P41 — geometry summary ("#5x5/8in-Screw005"; no construction recipe available for this part):
  bounding box: 15.9 x 6.0 x 6.0 mm
  tessellated surface: 3,812 triangles
  volume: 103 mm^3 (18% of its bounding box)
COMPONENT P42 — geometry summary ("#5x5/8in-Screw006"; no construction recipe available for this part):
  bounding box: 15.9 x 6.0 x 6.0 mm
  tessellated surface: 3,812 triangles
  volume: 103 mm^3 (18% of its bounding box)
COMPONENT P43 — geometry summary ("#5x5/8in-Screw007"; no construction recipe available for this part):
  bounding box: 15.9 x 6.0 x 6.0 mm
  tessellated surface: 3,812 triangles
  volume: 103 mm^3 (18% of its bounding box)
COMPONENT P44 — geometry summary ("#5x5/8in-Screw008"; no construction recipe available for this part):
  bounding box: 15.9 x 6.0 x 6.0 mm
  tessellated surface: 3,812 triangles
  volume: 103 mm^3 (18% of its bounding box)
COMPONENT P45 — geometry summary ("#5x5/8in-Screw009"; no construction recipe available for this part):
  bounding box: 15.9 x 6.0 x 6.0 mm
  tessellated surface: 3,812 triangles
  volume: 103 mm^3 (18% of its bounding box)
COMPONENT P46 — geometry summary ("#5x5/8in-Screw010"; no construction recipe available for this part):
  bounding box: 15.9 x 6.0 x 6.0 mm
  tessellated surface: 3,812 triangles
  volume: 103 mm^3 (18% of its bounding box)
COMPONENT P47 — geometry summary ("#5x5/8in-Screw011"; no construction recipe available for this part):
  bounding box: 15.9 x 6.0 x 6.0 mm
  tessellated surface: 3,812 triangles
  volume: 103 mm^3 (18% of its bounding box)
COMPONENT P48 — geometry summary ("#5x5/8in-Screw012"; no construction recipe available for this part):
  bounding box: 15.9 x 6.0 x 6.0 mm
  tessellated surface: 3,812 triangles
  volume: 103 mm^3 (18% of its bounding box)
COMPONENT P49 — geometry summary ("#5x5/8in-Screw013"; no construction recipe available for this part):
  bounding box: 15.9 x 6.0 x 6.0 mm
  tessellated surface: 3,812 triangles
  volume: 103 mm^3 (18% of its bounding box)
COMPONENT P50 — geometry summary ("#5x5/8in-Screw014"; no construction recipe available for this part):
  bounding box: 15.9 x 6.0 x 6.0 mm
  tessellated surface: 3,812 triangles
  volume: 103 mm^3 (18% of its bounding box)
COMPONENT P51 — geometry summary ("#5x5/8in-Screw015"; no construction recipe available for this part):
  bounding box: 15.9 x 6.0 x 6.0 mm
  tessellated surface: 3,812 triangles
  volume: 103 mm^3 (18% of its bounding box)
COMPONENT P52 — geometry summary ("#5x5/8in-Screw016"; no construction recipe available for this part):
  bounding box: 15.9 x 6.0 x 6.0 mm
  tessellated surface: 3,812 triangles
  volume: 103 mm^3 (18% of its bounding box)
COMPONENT P53 — geometry summary ("#5x5/8in-Screw017"; no construction recipe available for this part):
  bounding box: 15.9 x 6.0 x 6.0 mm
  tessellated surface: 3,812 triangles
  volume: 103 mm^3 (18% of its bounding box)
COMPONENT P54 — geometry summary ("#5x5/8in-Screw018"; no construction recipe available for this part):
  bounding box: 15.9 x 6.0 x 6.0 mm
  tessellated surface: 3,812 triangles
  volume: 103 mm^3 (18% of its bounding box)
COMPONENT P55 — geometry summary ("#5x5/8in-Screw019"; no construction recipe available for this part):
  bounding box: 15.9 x 6.0 x 6.0 mm
  tessellated surface: 3,812 triangles
  volume: 103 mm^3 (18% of its bounding box)
COMPONENT P56 — geometry summary ("#5x5/8in-Screw020"; no construction recipe available for this part):
  bounding box: 15.9 x 6.0 x 6.0 mm
  tessellated surface: 3,812 triangles
  volume: 103 mm^3 (18% of its bounding box)
COMPONENT P57 — geometry summary ("#5x5/8in-Screw021"; no construction recipe available for this part):
  bounding box: 15.9 x 6.0 x 6.0 mm
  tessellated surface: 3,812 triangles
  volume: 103 mm^3 (18% of its bounding box)
COMPONENT P58 — geometry summary ("#5x5/8in-Screw022"; no construction recipe available for this part):
  bounding box: 15.9 x 6.0 x 6.0 mm
  tessellated surface: 3,812 triangles
  volume: 103 mm^3 (18% of its bounding box)
COMPONENT P59 — geometry summary ("#5x5/8in-Screw023"; no construction recipe available for this part):
  bounding box: 15.9 x 6.0 x 6.0 mm
  tessellated surface: 3,812 triangles
  volume: 103 mm^3 (18% of its bounding box)
COMPONENT P60 — geometry summary ("#5x5/8in-Screw024"; no construction recipe available for this part):
  bounding box: 15.9 x 6.0 x 6.0 mm
  tessellated surface: 3,812 triangles
  volume: 103 mm^3 (18% of its bounding box)
COMPONENT P61 — geometry summary ("#5x5/8in-Screw025"; no construction recipe available for this part):
  bounding box: 15.9 x 6.0 x 6.0 mm
  tessellated surface: 3,812 triangles
  volume: 103 mm^3 (18% of its bounding box)
COMPONENT P62 — geometry summary ("#5x5/8in-Screw027"; no construction recipe available for this part):
  bounding box: 15.9 x 6.0 x 6.0 mm
  tessellated surface: 3,812 triangles
  volume: 103 mm^3 (18% of its bounding box)
COMPONENT P63 — geometry summary ("1/4in-Nut002"; no construction recipe available for this part):
  bounding box: 12.7 x 11.0 x 4.0 mm
  tessellated surface: 3,060 triangles
  volume: 313 mm^3 (56% of its bounding box)
COMPONENT P64 — geometry summary ("1/4in-Nut003"; no construction recipe available for this part):
  bounding box: 12.7 x 11.0 x 4.0 mm
  tessellated surface: 3,060 triangles
  volume: 313 mm^3 (56% of its bounding box)
COMPONENT P65 — geometry summary ("1/4in-Nut004"; no construction recipe available for this part):
  bounding box: 12.7 x 11.0 x 4.0 mm
  tessellated surface: 3,060 triangles
  volume: 313 mm^3 (56% of its bounding box)
COMPONENT P66 — geometry summary ("1/4in-Nut005"; no construction recipe available for this part):
  bounding box: 12.7 x 11.0 x 4.0 mm
  tessellated surface: 3,060 triangles
  volume: 313 mm^3 (56% of its bounding box)
COMPONENT P67 — geometry summary ("1/4inx1in-Screw002"; no construction recipe available for this part):
  bounding box: 29.2 x 14.6 x 14.5 mm
  tessellated surface: 12,510 triangles
  volume: 963 mm^3 (16% of its bounding box)
COMPONENT P68 — geometry summary ("1/4inx1in-Screw003"; no construction recipe available for this part):
  bounding box: 29.2 x 14.6 x 14.5 mm
  tessellated surface: 12,510 triangles
  volume: 963 mm^3 (16% of its bounding box)
COMPONENT P69 — geometry summary ("1/4inx1in-Screw004"; no construction recipe available for this part):
  bounding box: 29.2 x 14.6 x 14.5 mm
  tessellated surface: 12,510 triangles
  volume: 963 mm^3 (16% of its bounding box)
COMPONENT P70 — geometry summary ("1/4inx1in-Screw005"; no construction recipe available for this part):
  bounding box: 29.2 x 14.6 x 14.5 mm
  tessellated surface: 12,510 triangles
  volume: 963 mm^3 (16% of its bounding box)
PROVENANCE & LICENSES
A FreeCAD (.FCStd) document from a public repository crawl; recipes are the document's own serialized feature recipes (and, for linked parts, companion documents' recipes).
License: as declared in the source repository (recorded in the dataset sidecar).
